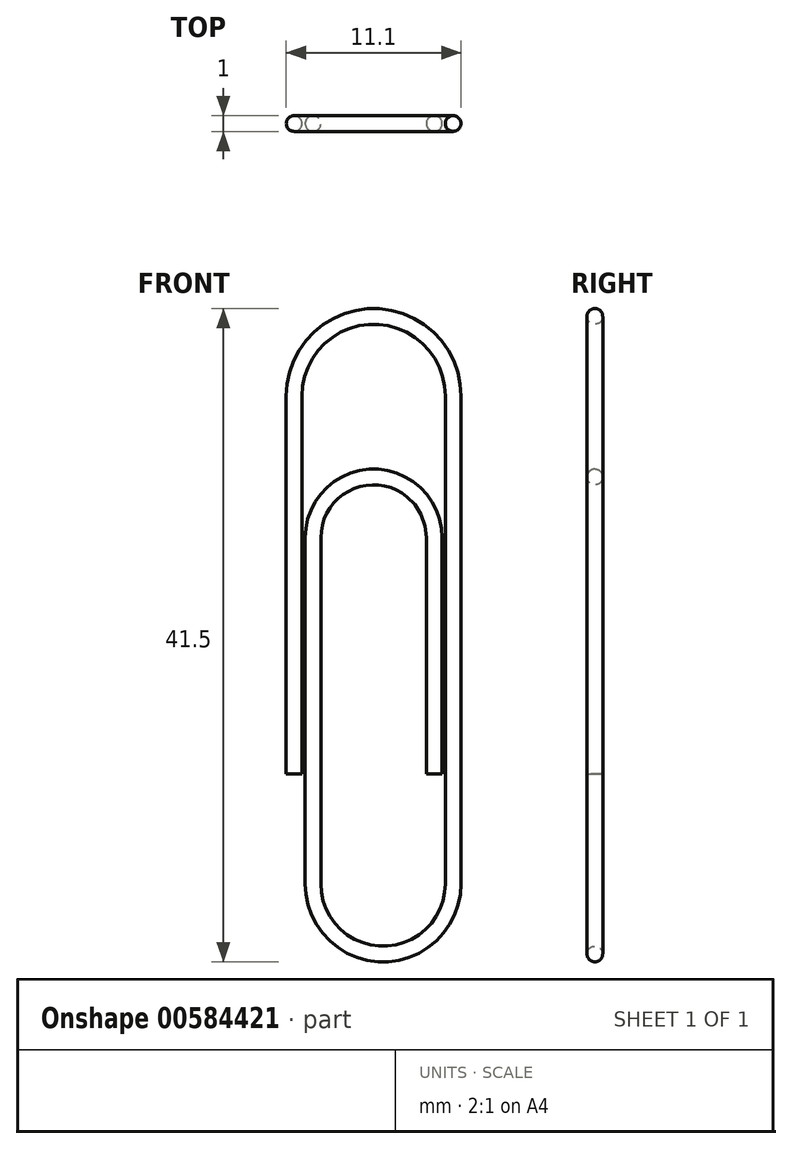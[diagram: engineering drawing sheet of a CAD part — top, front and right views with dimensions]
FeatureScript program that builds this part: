
annotation { "Feature Type Name" : "Feature", "Feature Type Description" : "" }
export const myFeature = defineFeature(function(context is Context, id is Id, definition is map)
    precondition{}
    {
        {
            var Q0;
            Q0=qCreatedBy(makeId("Front.planeOp"),FACE);
            var sketch = newSketch(context, id + "F0", { "sketchPlane" : qUnion([Q0])});
            skLineSegment(sketch, "E0", {"start": v(0, 0) * mm, "end": v(0, 15) * mm});
            skLineSegment(sketch, "E1", {"start": v(-7.7, 15) * mm, "end": v(-7.7, -7) * mm});
            skLineSegment(sketch, "E2", {"start": v(1.2, -7) * mm, "end": v(1.2, 24) * mm});
            skArc(sketch, "E3", {"start": v(0, 15) * mm, "mid": v(-3.85, 18.85) * mm, "end": v(-7.7, 15) * mm});
            skArc(sketch, "E4", {"start": v(-7.7, -7) * mm, "mid": v(-3.25, -11.45) * mm, "end": v(1.2, -7) * mm});
            skArc(sketch, "E5", {"start": v(1.2, 24) * mm, "mid": v(-3.85, 29.05) * mm, "end": v(-8.9, 24) * mm});
            skPoint(sketch, "E5.centerSnap0", {"position": v(-3.85, 18.85) * mm});
            skLineSegment(sketch, "E6", {"start": v(-8.9, 24) * mm, "end": v(-8.9, 0) * mm});
            skSolve(sketch);
        }
        {
            var Q0;
            Q0=qCreatedBy(makeId("Top.planeOp"),FACE);
            var sketch = newSketch(context, id + "F1", { "sketchPlane" : qUnion([Q0])});
            skCircle(sketch, "E7", {"center": v(0, 0) * mm, "radius": 0.5 * mm});
            skSolve(sketch);
        }
        {
            var Q0;
            Q0=makeQuery(id+"F1.imprint","IMPRINT",FACE,{"disambiguationData":[TD([[makeQuery(id+"F1.imprint","IMPRINT",EDGE,{"derivedFrom":sQuery(id+"F1.wireOp",EDGE,"E7")}),1.0]])]});
            var Q1;
            Q1=sQuery(id+"F0.wireOp",EDGE,"E0");
            var Q2;
            Q2=sQuery(id+"F0.wireOp",EDGE,"E3");
            var Q3;
            Q3=sQuery(id+"F0.wireOp",EDGE,"E1");
            var Q4;
            Q4=sQuery(id+"F0.wireOp",EDGE,"E4");
            var Q5;
            Q5=sQuery(id+"F0.wireOp",EDGE,"E2");
            var Q6;
            Q6=sQuery(id+"F0.wireOp",EDGE,"UmB4QFdj-4rJW-r6ty-CHEb-z6oz1IOP1jES");
            var Q7;
            Q7=sQuery(id+"F0.wireOp",EDGE,"cq8UUmGR-vIfg-l349-O6ND-LZ9xehZH6DQT");
            var Q8;
            Q8=sQuery(id+"F0.wireOp",EDGE,"E5");
            var Q9;
            Q9=sQuery(id+"F0.wireOp",EDGE,"E6");
            sweep(context, id + "F2", {"profiles" : qUnion([Q0]), "path" : qUnion([Q1, Q2, Q3, Q4, Q5, Q6, Q7, Q8, Q9])});
        }
    });
